# Revit family: Seating-LAMMHULTS-Add-Move-Stool_46
name_source: partatom
category: Furniture
revit_build: Autodesk Revit 2014 (Build: 20140709_2115(x64)
units: mm (PartAtom-declared; Revit-internal decimal feet)

## types (3) — shared parameters
Assembly Code = E2020
Depth = 560 mm  [stored 1.83727 ft]
Description = *Please enter mtrl description here for use in mto*
Height = 490 mm  [stored 1.60761 ft]
Keynote = 46.B
Manufacturer = LAMMHULTS
Model = ADD MOVE
URL = www.lammhults.se
Weight = 4.0
Width = 480 mm  [stored 1.5748 ft]

## per-type parameters (varying)
| type | Frame Material | Seat Material |
| Fabric - Red - Black | Metal - Black - Matte | Fabric - Rust Red Woven |
| Fabric - Red - Crome | Metal - Chrome - Polished | Fabric - Rust Red Woven |
| Plastic - Black | Metal - Black - Matte | Plastic - Black |

note: [stored X ft] marks values corroborated as IEEE doubles in the binary element streams (Revit-internal decimal feet)

## geometry (parser evidence)
native form markers: Blend x8, Sweep x1
no freeform markers — native parametric forms only
